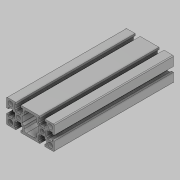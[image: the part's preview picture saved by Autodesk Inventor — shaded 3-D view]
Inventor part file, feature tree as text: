
AUTODESK INVENTOR PART (.ipt)
format: ipt  version: 2021.2 (Build 252289000, 289)  size: 289,792 bytes
history: native  units: in
note: dims shown in document units (in); Inventor stores cm internally (conversion verified against a paired STEP export)
features: other x3, extrude x1, sketch x1, projected_geometry x1
ambient origin geometry x8: Origin, YZ Plane, XZ Plane, XY Plane, X Axis, Y Axis, Z Axis, Center Point
bodies: Body1 (feature_tree)
feature tree (6):
  other  "AFS-3060-150"
  other  "ソリッド2"
  extrude  "押し出し1"  Depth=5.9055in
  sketch  "スケッチ2"
  projected_geometry  "投影ループ1"
  other  "ソリッド1"
